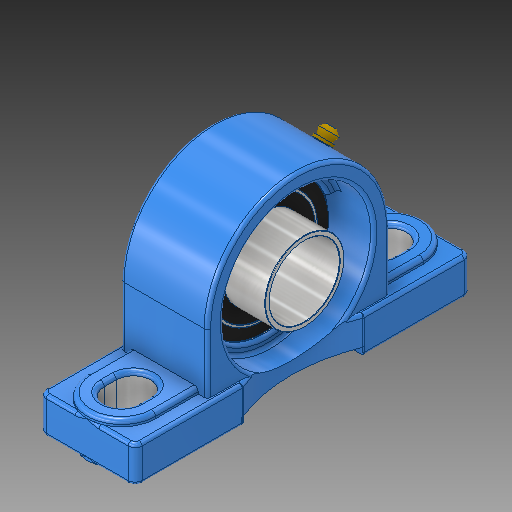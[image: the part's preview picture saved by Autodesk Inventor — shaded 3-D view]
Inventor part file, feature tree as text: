
AUTODESK INVENTOR PART (.ipt)
format: ipt  version: 2019 (Build 230136000, 136)  size: 688,640 bytes
history: native  units: in
note: dims shown in document units (in); Inventor stores cm internally (conversion verified against a paired STEP export)
features: sketch x28, plane x7, other x3
ambient origin geometry x8: Origin, YZ Plane, XZ Plane, XY Plane, X Axis, Y Axis, Z Axis, Center Point
bodies: Solid1 (feature_tree)
feature tree (38):
  other  "Pillow Bearing inventor_MIR.ipt"
  other  "Solid1::Pillow Bearing inventor_MIR.ipt"
  other  "TaggingFeature1"
  sketch  "Sketch1"  dims[d0=0.3937in]
  sketch  "Sketch2"
  sketch  "Sketch3"
  sketch  "Sketch4"
  sketch  "Sketch5"
  sketch  "Sketch6"
  sketch  "Sketch7"
  sketch  "Sketch8"
  sketch  "Sketch9"
  sketch  "Sketch10"
  sketch  "Sketch11"
  sketch  "Sketch13"
  sketch  "Sketch14"
  sketch  "Sketch15"
  sketch  "Sketch17"
  sketch  "Sketch18"
  sketch  "Sketch19"
  sketch  "Sketch20"
  sketch  "Sketch21"
  sketch  "Sketch22"
  sketch  "Sketch23"
  sketch  "Sketch24"
  sketch  "Sketch25"
  sketch  "Sketch26"
  sketch  "Sketch27"
  sketch  "Sketch28"
  sketch  "Sketch29"
  sketch  "Sketch30"
  plane  "Work Plane1"
  plane  "Work Plane2"
  plane  "Work Plane5"
  plane  "Work Plane6"
  plane  "Work Plane7"
  plane  "Work Plane8"
  plane  "Work Plane9"
